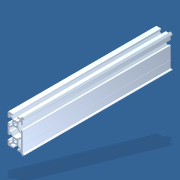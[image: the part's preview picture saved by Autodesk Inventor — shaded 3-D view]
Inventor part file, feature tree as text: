
AUTODESK INVENTOR PART (.ipt)
format: ipt  version: 2012 SP1 (Build 160190100, 190)  size: 435,712 bytes
history: native  units: in
note: dims shown in document units (in); Inventor stores cm internally (conversion verified against a paired STEP export)
features: other x1, imported_body x1, extrude x1, sketch x1
ambient origin geometry x8: Origin, YZ Plane, XZ Plane, XY Plane, X Axis, Y Axis, Z Axis, Center Point
feature tree (4):
  other  "MAKER_SLIDE_6_100"
  imported_body  "Base1"
  extrude  "Extrusion2"  [1 undecoded]
  sketch  "Sketch2"  dims[d2=3.937in d3=0.0in]
note: 1 required parameter value undecoded (feature->parameter linkage not recoverable at this tier; creation-order binding heuristic only, values carry confidence <= 0.55)
